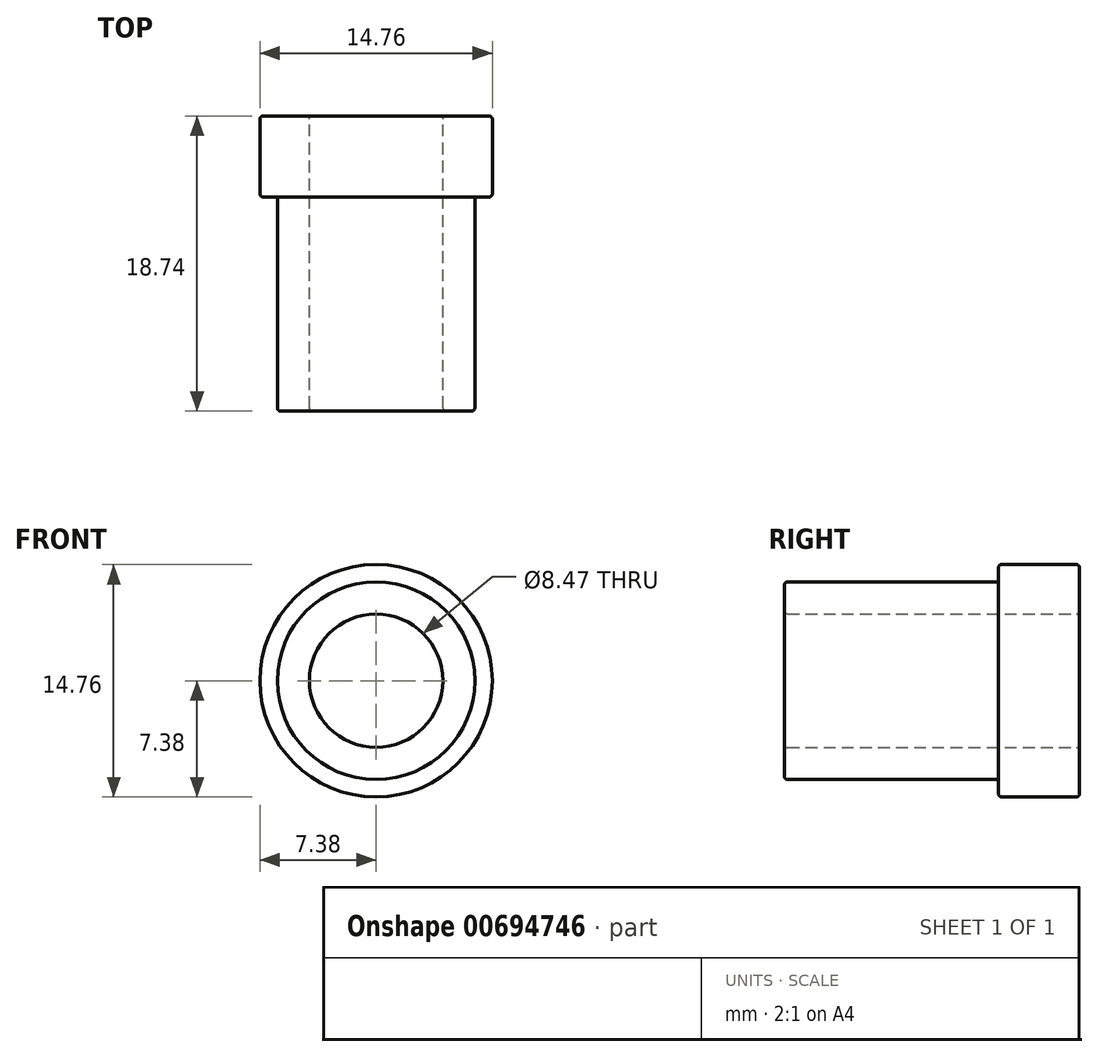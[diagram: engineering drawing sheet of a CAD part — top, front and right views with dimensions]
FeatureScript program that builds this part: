
annotation { "Feature Type Name" : "Feature", "Feature Type Description" : "" }
export const myFeature = defineFeature(function(context is Context, id is Id, definition is map)
    precondition{}
    {
        {
            var Q0;
            Q0=qCreatedBy(makeId("Front.planeOp"),FACE);
            var sketch = newSketch(context, id + "F0", { "sketchPlane" : qUnion([Q0])});
            skCircle(sketch, "E0", {"center": v(0, 0) * mm, "radius": 7.38 * mm});
            skCircle(sketch, "E1", {"center": v(0, 0) * mm, "radius": 4.24 * mm});
            skSolve(sketch);
        }
        {
            var Q0;
            Q0=makeQuery(id+"F0.imprint","IMPRINT",FACE,{"disambiguationData":[TD([[makeQuery(id+"F0.imprint","IMPRINT",EDGE,{"derivedFrom":sQuery(id+"F0.wireOp",EDGE,"E0")}),1.0]])]});
            extrude(context, id + "F1", {"entities" : qUnion([Q0]), "depth" : 5.14 * mm, "offsetDistance" : 25 * mm});
        }
        {
            var Q0;
            Q0=makeQuery(id+"F1.opExtrude","CAP_FACE",FACE,{"disambiguationData":[OSD([sQuery(id+"F0.wireOp",EDGE,"E0"),sQuery(id+"F0.wireOp",EDGE,"E1")])],"isStart":false});
            var sketch = newSketch(context, id + "F2", { "sketchPlane" : qUnion([Q0])});
            skCircle(sketch, "E2", {"center": v(0, 0) * mm, "radius": 4.24 * mm});
            skCircle(sketch, "E3", {"center": v(0, 0) * mm, "radius": 6.27 * mm});
            skSolve(sketch);
        }
        {
            var Q0;
            Q0=makeQuery(id+"F2.imprint","IMPRINT",FACE,{"disambiguationData":[TD([[makeQuery(id+"F2.imprint","IMPRINT",EDGE,{"derivedFrom":sQuery(id+"F2.wireOp",EDGE,"E2")}),-1.0]])]});
            extrude(context, id + "F3", {"entities" : qUnion([Q0]), "operationType" : NewBodyOperationType.ADD, "depth" : 13.6 * mm, "offsetDistance" : 25 * mm});
        }
        {
            var Q0;
            Q0=makeQuery(id+"F3.opExtrude","CAP_EDGE",EDGE,{"disambiguationData":[OSD([sQuery(id+"F2.wireOp",EDGE,"E3")])],"isStart":false});
            var Q1;
            Q1=makeQuery(id+"F1.opExtrude","CAP_EDGE",EDGE,{"disambiguationData":[OSD([sQuery(id+"F0.wireOp",EDGE,"E0")])],"isStart":false});
            var Q2;
            Q2=makeQuery(id+"F1.opExtrude","CAP_EDGE",EDGE,{"disambiguationData":[OSD([sQuery(id+"F0.wireOp",EDGE,"E0")])],"isStart":true});
            var Q3;
            Q3=makeQuery(id+"F3.opExtrude","CAP_EDGE",EDGE,{"disambiguationData":[OSD([sQuery(id+"F2.wireOp",EDGE,"E2")])],"isStart":false});
            var Q4;
            Q4=makeQuery(id+"F3.opExtrude","CAP_EDGE",EDGE,{"disambiguationData":[OSD([sQuery(id+"F2.wireOp",EDGE,"E3")])],"isStart":true});
            var Q5;
            Q5=makeQuery(id+"F1.opExtrude","CAP_EDGE",EDGE,{"disambiguationData":[OSD([sQuery(id+"F0.wireOp",EDGE,"E1")])],"isStart":true});
            fillet(context, id + "F4", {"entities" : qUnion([Q0, Q1, Q2, Q3, Q4, Q5]), "radius" : .2 * mm, "tangentPropagation" : true, "allowEdgeOverflow" : false});
        }
    });
